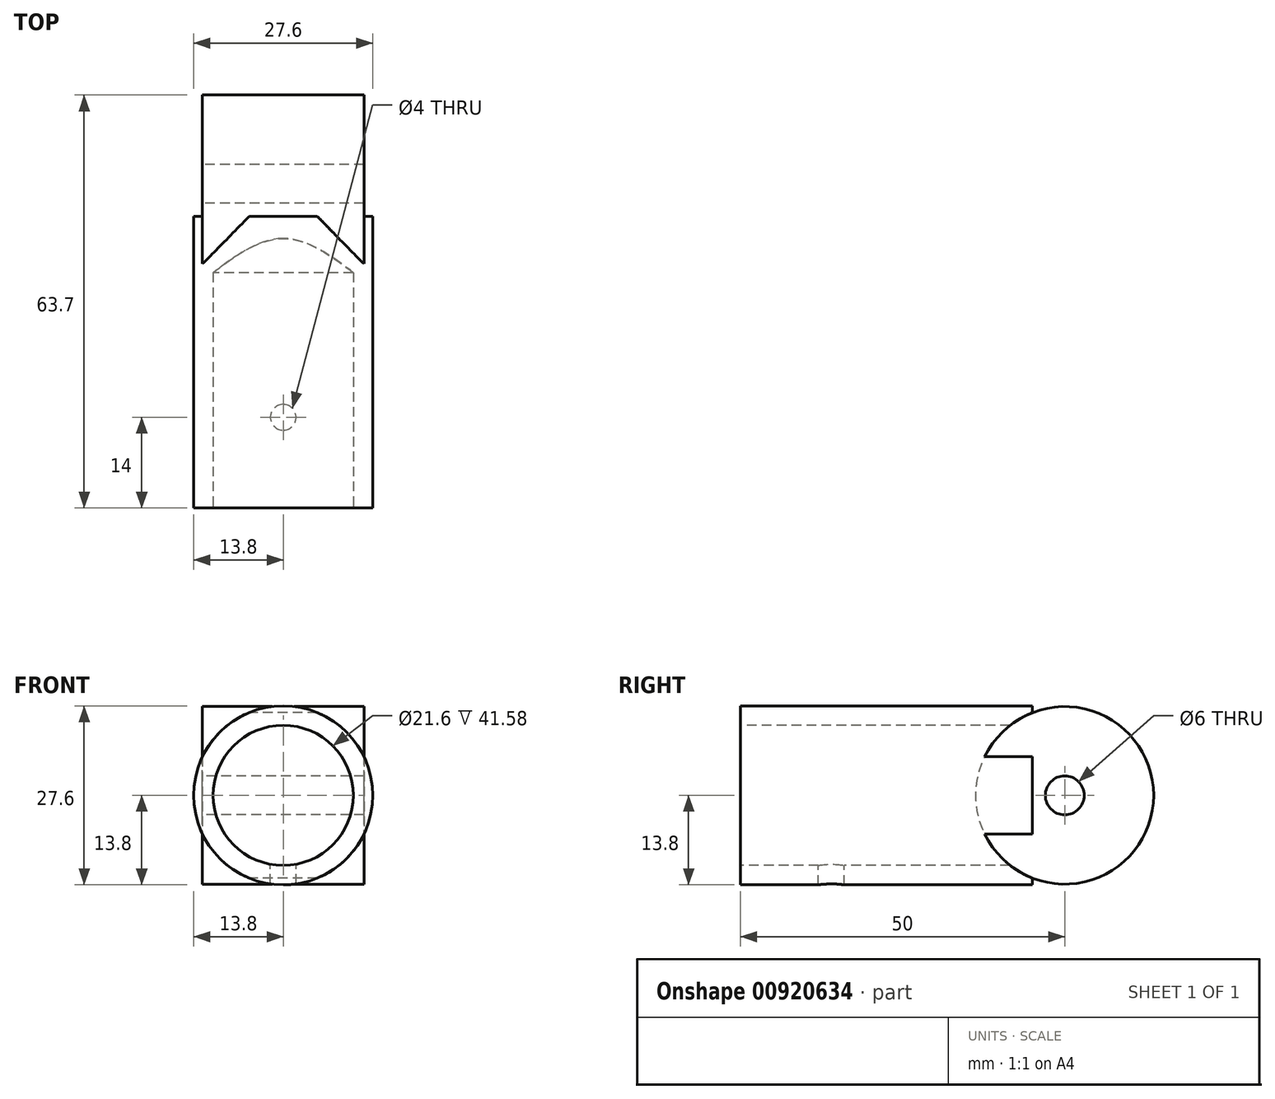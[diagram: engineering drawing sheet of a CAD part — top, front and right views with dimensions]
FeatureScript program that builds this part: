
annotation { "Feature Type Name" : "Feature", "Feature Type Description" : "" }
export const myFeature = defineFeature(function(context is Context, id is Id, definition is map)
    precondition{}
    {
        {
            var Q0;
            Q0=qCreatedBy(makeId("Front.planeOp"),FACE);
            cPlane(context, id + "F0", {"entities" : qUnion([Q0]), "cplaneType" : CPlaneType.OFFSET, "offset" : 50 * mm, "width" : 150 * mm, "height" : 150 * mm});
        }
        {
            var Q0;
            Q0=qCreatedBy(id+"F0.planeOp",FACE);
            var sketch = newSketch(context, id + "F1", { "sketchPlane" : qUnion([Q0])});
            skCircle(sketch, "E0", {"center": v(0, 0) * mm, "radius": 13.8 * mm});
            skCircle(sketch, "E1", {"center": v(0, 0) * mm, "radius": 10.8 * mm});
            skSolve(sketch);
        }
        {
            var Q0;
            Q0=qCreatedBy(makeId("Right.planeOp"),FACE);
            var sketch = newSketch(context, id + "F2", { "sketchPlane" : qUnion([Q0])});
            skCircle(sketch, "E2", {"center": v(0, 0) * mm, "radius": 13.7 * mm});
            skCircle(sketch, "E3", {"center": v(0, 0) * mm, "radius": 3 * mm});
            skSolve(sketch);
        }
        {
            var Q0;
            Q0=makeQuery(id+"F2.imprint","IMPRINT",FACE,{"disambiguationData":[TD([[makeQuery(id+"F2.imprint","IMPRINT",EDGE,{"derivedFrom":sQuery(id+"F2.wireOp",EDGE,"E2")}),1.0]])]});
            extrude(context, id + "F3", {"entities" : qUnion([Q0]), "endBound" : BoundingType.SYMMETRIC, "depth" : 24.9 * mm, "offsetDistance" : 25 * mm});
        }
        {
            var Q0;
            Q0=makeQuery(id+"F1.imprint","IMPRINT",FACE,{"disambiguationData":[TD([[makeQuery(id+"F1.imprint","IMPRINT",EDGE,{"derivedFrom":sQuery(id+"F1.wireOp",EDGE,"E0")}),1.0]])]});
            extrude(context, id + "F4", {"entities" : qUnion([Q0]), "operationType" : NewBodyOperationType.ADD, "oppositeDirection" : true, "depth" : 45 * mm, "offsetDistance" : 25 * mm});
        }
        {
            var Q0;
            Q0=qCreatedBy(makeId("Top.planeOp"),FACE);
            var sketch = newSketch(context, id + "F5", { "sketchPlane" : qUnion([Q0])});
            skLineSegment(sketch, "E4", {"start": v(0, 0) * mm, "end": v(0, -36) * mm, "construction": true});
            skSolve(sketch);
        }
        {
            var Q0;
            Q0=sQuery(id+"F5.wireOp",VERTEX,"E4.end");
            var Q1;
            Q1=makeQuery(id+"F3.opExtrude","SWEPT_BODY",BODY,{"disambiguationData":[OSD([sQuery(id+"F2.wireOp",EDGE,"E2"),sQuery(id+"F2.wireOp",EDGE,"E3")])]});
            hole(context, id + "F6", {"style" : HoleStyle.SIMPLE, "endStyle" : HoleEndStyle.THROUGH, "holeDiameter" : 4 * mm, "majorDiameter" : 5 * mm, "isTappedThrough" : true, "tappedDepth" : 12 * mm, "tapClearance" : 3, "locations" : qUnion([Q0]), "scope" : qUnion([Q1])});
        }
    });
